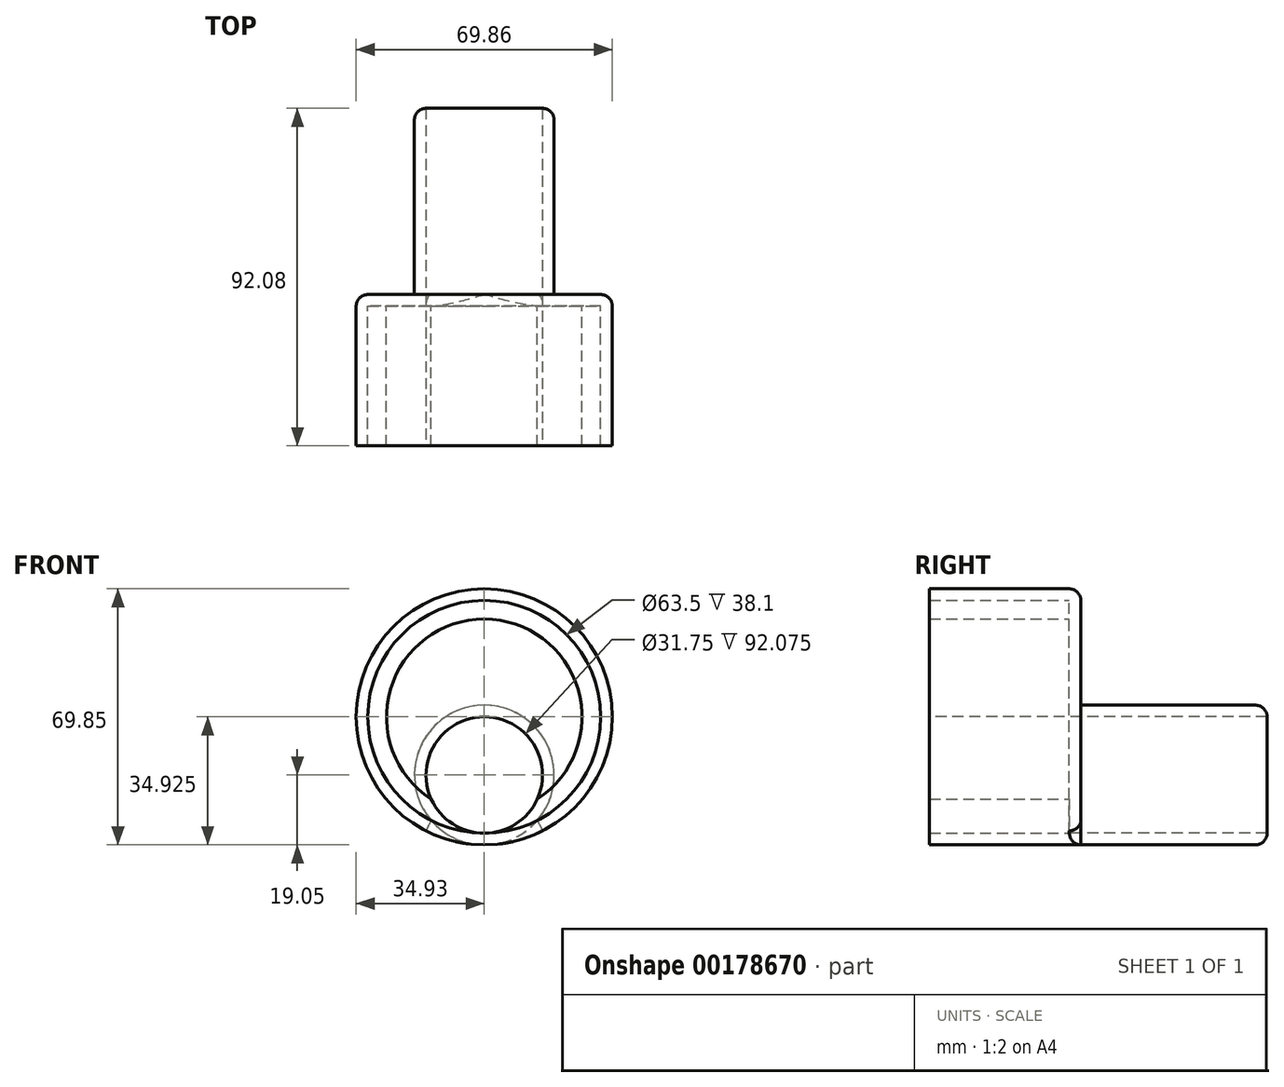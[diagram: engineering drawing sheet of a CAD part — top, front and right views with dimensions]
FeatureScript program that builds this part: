
annotation { "Feature Type Name" : "Feature", "Feature Type Description" : "" }
export const myFeature = defineFeature(function(context is Context, id is Id, definition is map)
    precondition{}
    {
        {
            var Q0;
            Q0=qCreatedBy(makeId("Front.planeOp"),FACE);
            var sketch = newSketch(context, id + "F0", { "sketchPlane" : qUnion([Q0])});
            skCircle(sketch, "E0", {"center": v(0, 34.92) * mm, "radius": 34.92 * mm});
            skCircle(sketch, "E1", {"center": v(0, 34.92) * mm, "radius": 31.75 * mm});
            skSolve(sketch);
        }
        {
            var Q0;
            Q0=makeQuery(id+"F0.imprint","IMPRINT",FACE,{"disambiguationData":[TD([[makeQuery(id+"F0.imprint","IMPRINT",EDGE,{"derivedFrom":sQuery(id+"F0.wireOp",EDGE,"E0")}),1.0]])]});
            extrude(context, id + "F1", {"entities" : qUnion([Q0]), "depth" : 38.1 * mm});
        }
        {
            var Q0;
            Q0=qCreatedBy(makeId("Front.planeOp"),FACE);
            var sketch = newSketch(context, id + "F2", { "sketchPlane" : qUnion([Q0])});
            skCircle(sketch, "E2", {"center": v(0, 34.92) * mm, "radius": 34.92 * mm});
            skSolve(sketch);
        }
        {
            var Q0;
            Q0=makeQuery(id+"F2.imprint","IMPRINT",FACE,{"disambiguationData":[TD([[makeQuery(id+"F2.imprint","IMPRINT",EDGE,{"derivedFrom":sQuery(id+"F2.wireOp",EDGE,"E2")}),1.0]])]});
            extrude(context, id + "F3", {"entities" : qUnion([Q0]), "operationType" : NewBodyOperationType.ADD, "oppositeDirection" : true, "depth" : 3.17 * mm});
        }
        {
            var Q0;
            Q0=makeQuery(id+"F3.opExtrude","CAP_FACE",FACE,{"disambiguationData":[OSD([sQuery(id+"F2.wireOp",EDGE,"E2")])],"isStart":false});
            var sketch = newSketch(context, id + "F4", { "sketchPlane" : qUnion([Q0])});
            skCircle(sketch, "E3", {"center": v(0, 19.05) * mm, "radius": 19.05 * mm});
            skCircle(sketch, "E4", {"center": v(0, 19.05) * mm, "radius": 15.88 * mm});
            skSolve(sketch);
        }
        {
            var Q0;
            Q0 = qSketchRegion(id + "F4", true);
            extrude(context, id + "F5", {"entities" : qUnion([Q0]), "operationType" : NewBodyOperationType.ADD, "depth" : 50.8 * mm});
        }
        {
            var Q0;
            Q0=makeQuery(id+"F5.boolean.opBoolean","SPLIT",FACE,{"disambiguationData":[TD([makeQuery(id+"F5.opExtrude","SWEPT_FACE",FACE,{"disambiguationData":[OSD([sQuery(id+"F4.wireOp",EDGE,"E4")])]})])],"derivedFrom":makeQuery(id+"F3.opExtrude","CAP_FACE",FACE,{"disambiguationData":[OSD([sQuery(id+"F2.wireOp",EDGE,"E2")])],"isStart":false})});
            extrude(context, id + "F6", {"entities" : qUnion([Q0]), "operationType" : NewBodyOperationType.REMOVE, "endBound" : BoundingType.THROUGH_ALL, "oppositeDirection" : true, "depth" : 19.3 * mm});
        }
        {
            var Q0;
            Q0=makeQuery(id+"F5.opExtrude","CAP_EDGE",EDGE,{"disambiguationData":[OSD([sQuery(id+"F4.wireOp",EDGE,"E3")])],"isStart":false});
            fillet(context, id + "F7", {"entities" : qUnion([Q0]), "radius" : 3.17 * mm, "tangentPropagation" : true, "allowEdgeOverflow" : false});
        }
        {
            var Q0;
            Q0=makeQuery(id+"F3.opExtrude","CAP_EDGE",EDGE,{"disambiguationData":[OSD([sQuery(id+"F2.wireOp",EDGE,"E2")])],"isStart":false});
            fillet(context, id + "F8", {"entities" : qUnion([Q0]), "radius" : 3.17 * mm, "tangentPropagation" : true, "allowEdgeOverflow" : false});
        }
        {
            var Q0;
            Q0=makeQuery(id+"F3.opExtrude","CAP_FACE",FACE,{"disambiguationData":[OSD([sQuery(id+"F2.wireOp",EDGE,"E2")])],"isStart":true});
            var sketch = newSketch(context, id + "F9", { "sketchPlane" : qUnion([Q0])});
            skCircle(sketch, "E5", {"center": v(0, 34.92) * mm, "radius": 26.67 * mm});
            skSolve(sketch);
        }
        {
            var Q0;
            {var subQ0=sQuery(id+"F9.wireOp",EDGE,"E5");var subQ1=makeQuery(id+"F6.boolean.opBoolean","INTERSECT",EDGE,{"derivedFrom":[makeQuery(id+"F3.opExtrude","CAP_FACE",FACE,{"disambiguationData":[OSD([sQuery(id+"F2.wireOp",EDGE,"E2")])],"isStart":true}),makeQuery(id+"F6.opExtrude","SWEPT_FACE",FACE,{"disambiguationData":[OSD([sQuery(id+"F4.wireOp",EDGE,"E4")])]})]});var subQ2=makeQuery(id+"F9.imprint","INTERSECT",VERTEX,{"disambiguationData":[OD(0.0)],"derivedFrom":[subQ1,subQ0]});Q0=makeQuery(id+"F9.imprint","IMPRINT",FACE,{"disambiguationData":[TD([[makeQuery(id+"F9.imprint","IMPRINT",EDGE,{"disambiguationData":[TD([[subQ2,1.0]])],"derivedFrom":subQ0}),1.0]])]});}
            var Q1;
            {var subQ0=sQuery(id+"F0.wireOp",EDGE,"E1");var subQ1=sQuery(id+"F0.wireOp",EDGE,"E0");Q1=makeQuery(id+"F1lhKfY3F3Cyyd8_1.boolean.opBoolean","MERGE",FACE,{"derivedFrom":[makeQuery(id+"F1.opExtrude","CAP_FACE",FACE,{"disambiguationData":[OSD([subQ1,subQ0])],"isStart":false}),makeQuery(id+"F1lhKfY3F3Cyyd8_1.opExtrude","CAP_FACE",FACE,{"disambiguationData":[OSD([subQ1,subQ0])],"isStart":false})]});}
            extrude(context, id + "F10", {"entities" : qUnion([Q0]), "operationType" : NewBodyOperationType.ADD, "endBound" : BoundingType.UP_TO_SURFACE, "endBoundEntityFace" : qUnion([Q1]), "depth" : 25.4 * mm});
        }
    });
